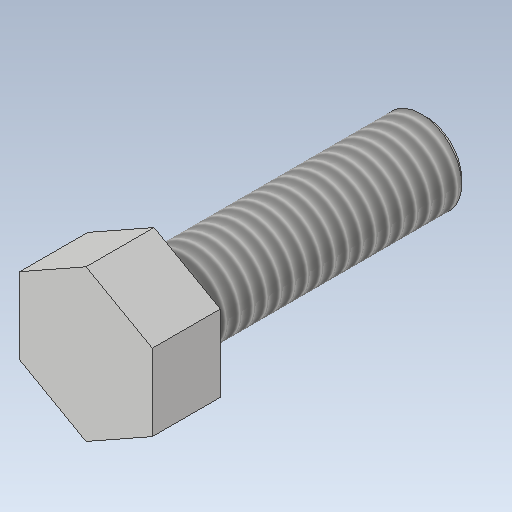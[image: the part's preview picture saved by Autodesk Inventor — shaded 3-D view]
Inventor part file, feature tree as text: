
AUTODESK INVENTOR PART (.ipt)
format: ipt  version: 2020 (Build 240168000, 168)  size: 143,872 bytes
history: native  units: mm
features: extrude x2, sketch x2, other x1, thread x1, chamfer x1
ambient origin geometry x8: Origin, YZ Plane, XZ Plane, XY Plane, X Axis, Y Axis, Z Axis, Center Point
bodies: Body1 (feature_tree)
feature tree (7):
  other  "Твердое тело1"
  extrude  "Выдавливание1"  Depth=4.0mm TaperAngle=0.0deg
  extrude  "Выдавливание2"  Depth=4.8mm
  thread  "Резьба1"
  chamfer  "Фаска1"  Distance=16.0mm
  sketch  "Эскиз1"
  sketch  "Эскиз2"
